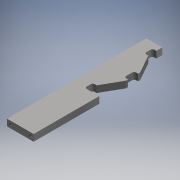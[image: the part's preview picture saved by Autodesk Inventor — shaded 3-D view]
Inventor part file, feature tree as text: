
AUTODESK INVENTOR PART (.ipt)
format: ipt  version: 2018 (Build 220112000, 112)  size: 169,472 bytes
history: native  units: mm
features: extrude x3, hole x1
ambient origin geometry x8: Origin, YZ Plane, XZ Plane, XY Plane, X Axis, Y Axis, Z Axis, Center Point
bodies: Volumenkörper1 (feature_tree)
feature tree (4):
  extrude  "Extrusion1"  Depth=210.0mm
  extrude  "Extrusion2"  Depth=40.0mm
  extrude  "Extrusion3"  Depth=10.0mm TaperAngle=0.0deg
  hole  "Bohrung1"  [1 undecoded]
note: 1 required parameter value undecoded (feature->parameter linkage not recoverable at this tier; creation-order binding heuristic only, values carry confidence <= 0.55)
